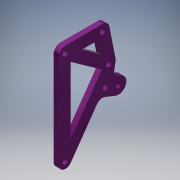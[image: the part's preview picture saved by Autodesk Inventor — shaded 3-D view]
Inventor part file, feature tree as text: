
AUTODESK INVENTOR PART (.ipt)
format: ipt  version: 2017 SP1 (Build 210196100, 196)  size: 181,760 bytes
history: native  units: in
note: dims shown in document units (in); Inventor stores cm internally (conversion verified against a paired STEP export)
features: extrude x2, sketch x2, projected_geometry x1
ambient origin geometry x8: Origin, YZ Plane, XZ Plane, XY Plane, X Axis, Y Axis, Z Axis, Center Point
bodies: Solid1 (feature_tree)
feature tree (5):
  extrude  "Extrusion1"  Depth=0.26in
  extrude  "Extrusion2"  Depth=0.25in
  sketch  "Sketch1"  dims[d0=1.0in d1=0.26in]
  sketch  "Sketch5"  dims[d2=0.548in d3=1.25in d4=1.5in d5=3.0in d7=0.25in d8=0.0in d10=1.0in d14=0.25in d48=0.25in d57=0.1875in d58=0.0in d59=0.1875in d62=0.875in d63=0.875in d66=1.5in d67=0.2in d68=0.25in d69=0.25in]
  projected_geometry  "Projected Loop1"
